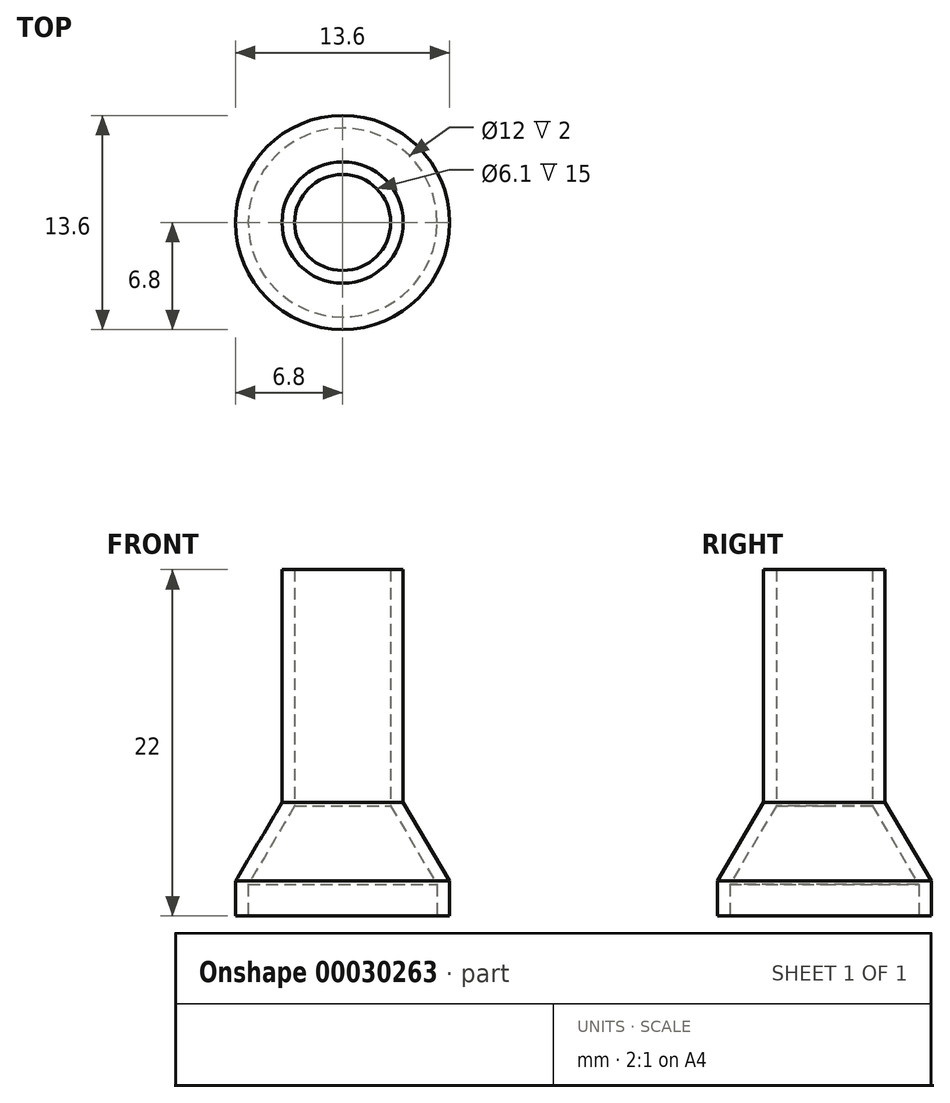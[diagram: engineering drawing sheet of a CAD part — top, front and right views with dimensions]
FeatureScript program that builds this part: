
annotation { "Feature Type Name" : "Feature", "Feature Type Description" : "" }
export const myFeature = defineFeature(function(context is Context, id is Id, definition is map)
    precondition{}
    {
        {
            var Q0;
            Q0=qCreatedBy(makeId("Front.planeOp"),FACE);
            var sketch = newSketch(context, id + "F0", { "sketchPlane" : qUnion([Q0])});
            skLineSegment(sketch, "E0", {"start": v(-6, 0) * mm, "end": v(-6, 2) * mm});
            skLineSegment(sketch, "E1", {"start": v(-6, 2) * mm, "end": v(-3.05, 7) * mm});
            skLineSegment(sketch, "E2", {"start": v(-3.05, 7) * mm, "end": v(-3.05, 22) * mm});
            skLineSegment(sketch, "E3", {"start": v(-3.05, 22) * mm, "end": v(0, 22) * mm});
            skLineSegment(sketch, "E4", {"start": v(-6, 0) * mm, "end": v(0, 0) * mm});
            skLineSegment(sketch, "E5", {"start": v(0, 0) * mm, "end": v(0, 22) * mm});
            skLineSegment(sketch, "E6.0", {"start": v(-3.85, 7.22) * mm, "end": v(-3.85, 22) * mm});
            skLineSegment(sketch, "E6.1", {"start": v(-6.8, 2.22) * mm, "end": v(-3.85, 7.22) * mm});
            skLineSegment(sketch, "E6.2", {"start": v(-6.8, 0) * mm, "end": v(-6.8, 2.22) * mm});
            skLineSegment(sketch, "E7", {"start": v(-3.85, 22) * mm, "end": v(-3.05, 22) * mm});
            skLineSegment(sketch, "E8", {"start": v(-6.8, 0) * mm, "end": v(-6, 0) * mm});
            skSolve(sketch);
        }
        {
            var Q0;
            Q0=makeQuery(id+"F0.imprint","IMPRINT",FACE,{"disambiguationData":[TD([[makeQuery(id+"F0.imprint","IMPRINT",EDGE,{"derivedFrom":sQuery(id+"F0.wireOp",EDGE,"E0")}),1.0]])]});
            var Q1;
            Q1=sQuery(id+"F0.wireOp",EDGE,"E5");
            revolve(context, id + "F1", {"entities" : qUnion([Q0]), "axis" : qUnion([Q1]), "revolveType" : RevolveType.FULL});
        }
    });
